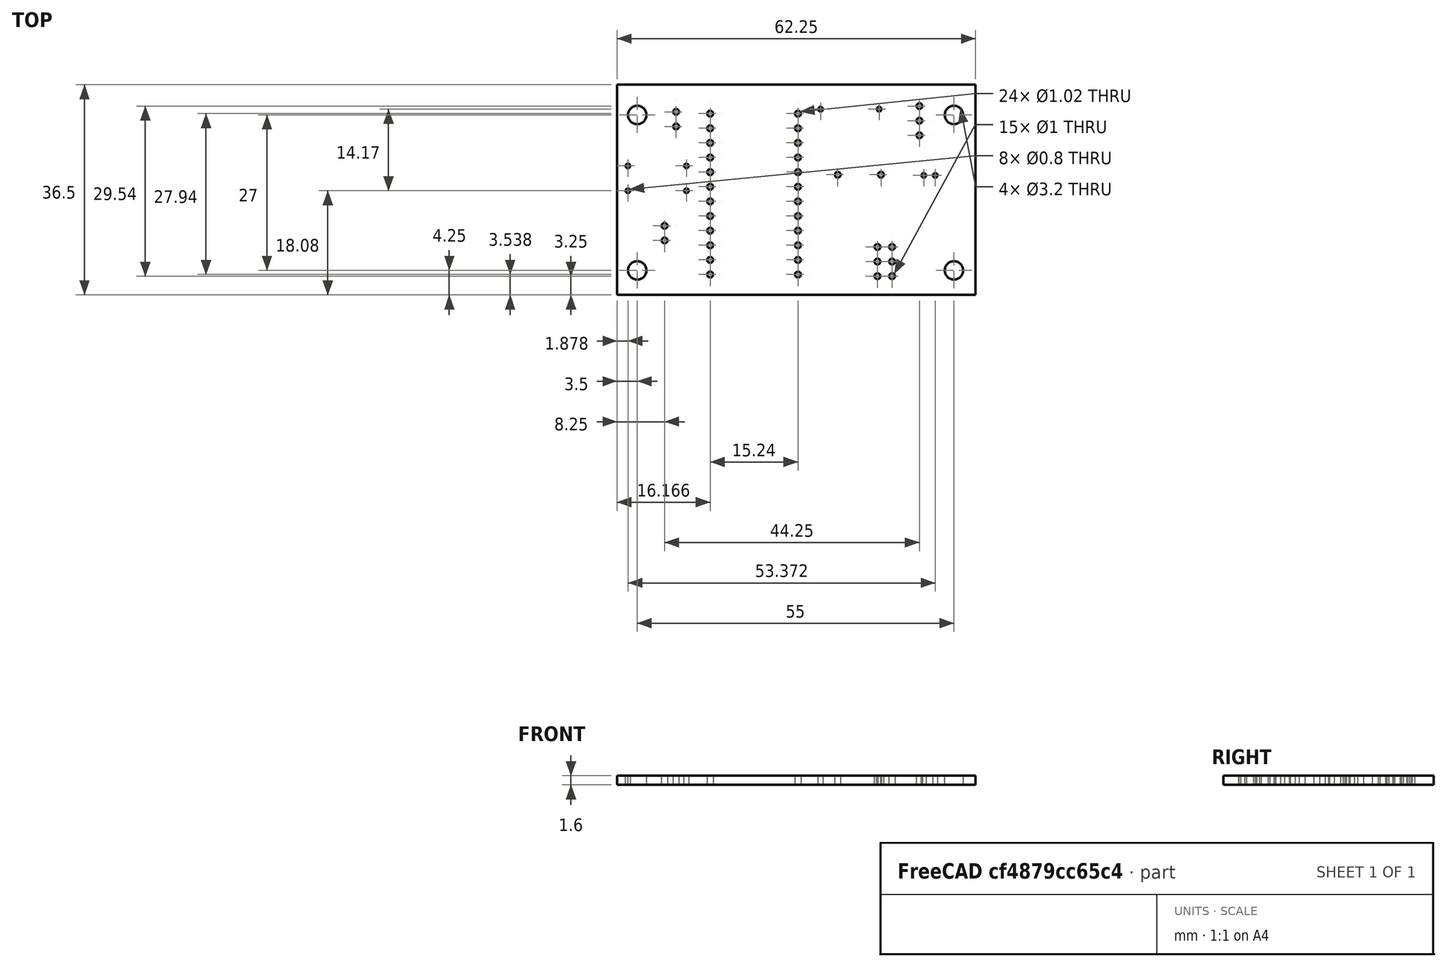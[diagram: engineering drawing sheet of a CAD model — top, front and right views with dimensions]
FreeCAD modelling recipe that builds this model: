
FCSTD DOCUMENT  (FreeCAD 0.18.4R)
Label: pcbstepup
License: All rights reserved
LicenseURL: http://en.wikipedia.org/wiki/All_rights_reserved
objects: App::Part×3, PartDesign::CoordinateSystem×1, Part::Feature×1, Sketcher::SketchObject×1
note: 3 computed .brp shape members not serialized (recipe doc carries the construction recipe); baked Part::Feature solids carry a one-line shape summary decoded from their .brp

FEATURE [PartDesign::CoordinateSystem] Local_CS
  AttacherType = Attacher::AttachEngine3D
FEATURE [Part::Feature] Pcb
  Placement = pos=(-148.5,98.5,0) rot=(0,0,1;0rad)
  shape: bbox 62.25 x 36.5 x 1.6 mm, 58 faces (baked)
FEATURE [Sketcher::SketchObject] PCB_Sketch
  sketch-geometry (5):
    g0: LineSegment StartX=15.25 StartY=26.75 StartZ=0 EndX=-27.5 EndY=26.75 EndZ=0
    g1: LineSegment StartX=15.25 StartY=-9.75 StartZ=0 EndX=15.25 EndY=26.75 EndZ=0
    g2: LineSegment StartX=-47 StartY=-9.75 StartZ=0 EndX=15.25 EndY=-9.75 EndZ=0
    g3: LineSegment StartX=-47 StartY=26.75 StartZ=0 EndX=-47 EndY=-9.75 EndZ=0
    g4: LineSegment StartX=-27.5 StartY=26.75 StartZ=0 EndX=-47 EndY=26.75 EndZ=0
  constraints (5):
    c: Coincident(g2,g3)
    c: Coincident(g3,g4)
    c: Coincident(g0,g4)
    c: Coincident(g1,g2)
    c: Coincident(g0,g1)
FEATURE [App::Part] Board_Geoms
  Group = -> [Local_CS,Pcb,PCB_Sketch]
  Origin = -> Origin
FEATURE [App::Part] Step_Models
  Origin = -> Origin002
FEATURE [App::Part] Board  label="pro_micro_audio"
  Group = -> [Board_Geoms,Step_Models]
  Origin = -> Origin001
